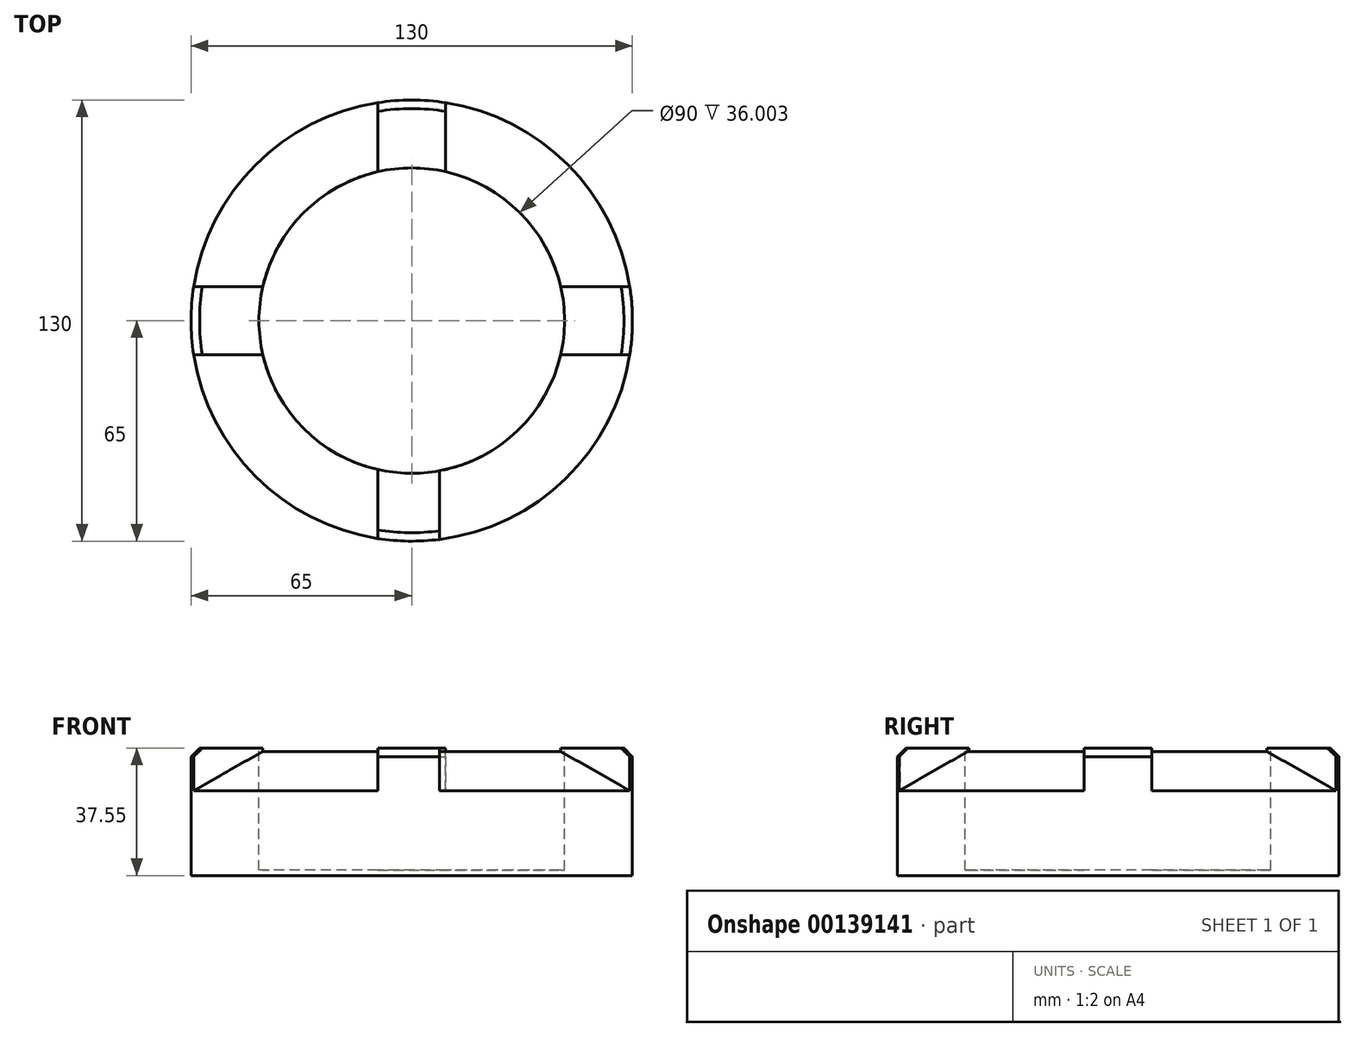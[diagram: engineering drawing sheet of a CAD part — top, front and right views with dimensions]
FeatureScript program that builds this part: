
annotation { "Feature Type Name" : "Feature", "Feature Type Description" : "" }
export const myFeature = defineFeature(function(context is Context, id is Id, definition is map)
    precondition{}
    {
        {
            var Q0;
            Q0=qCreatedBy(makeId("Right.planeOp"),FACE);
            var sketch = newSketch(context, id + "F0", { "sketchPlane" : qUnion([Q0])});
            skLineSegment(sketch, "E0", {"start": v(0, 0) * mm, "end": v(-65, 0) * mm});
            skLineSegment(sketch, "E1", {"start": v(0, 0) * mm, "end": v(-45, 0) * mm});
            skPoint(sketch, "E2", {"position": v(-45, 11.55) * mm});
            skLineSegment(sketch, "E3", {"start": v(-45, 11.55) * mm, "end": v(0, 11.55) * mm});
            skLineSegment(sketch, "E4", {"start": v(0, 11.55) * mm, "end": v(0, 0) * mm});
            skLineSegment(sketch, "E5", {"start": v(-65, 0) * mm, "end": v(-45, 11.55) * mm});
            skSolve(sketch);
        }
        {
            var Q0;
            {var subQ2=sQuery(id+"F0.wireOp",EDGE,"E0");Q0=makeQuery(id+"F0.imprint","IMPRINT",FACE,{"disambiguationData":[TD([[makeQuery(id+"F0.imprint","IMPRINT",EDGE,{"derivedFrom":subQ2}),-1.0]])]});}
            var Q1;
            Q1=sQuery(id+"F0.wireOp",EDGE,"E4");
            revolve(context, id + "F1", {"entities" : qUnion([Q0]), "axis" : qUnion([Q1]), "revolveType" : RevolveType.FULL});
        }
        {
            var Q0;
            Q0=makeQuery(id+"F1.opRevolve","SWEPT_FACE",FACE,{"disambiguationData":[OSD([sQuery(id+"F0.wireOp",EDGE,"E0"),sQuery(id+"F0.wireOp",EDGE,"E1")])]});
            extrude(context, id + "F2", {"entities" : qUnion([Q0]), "operationType" : NewBodyOperationType.ADD, "depth" : 25 * mm});
        }
        {
            var Q0;
            Q0=makeQuery(id+"F1.opRevolve","SWEPT_FACE",FACE,{"disambiguationData":[OSD([sQuery(id+"F0.wireOp",EDGE,"E3")])]});
            extrude(context, id + "F3", {"entities" : qUnion([Q0]), "operationType" : NewBodyOperationType.REMOVE, "oppositeDirection" : true, "depth" : 35 * mm});
        }
        {
            var Q0;
            Q0=makeQuery(id+"F2.opExtrude","CAP_FACE",FACE,{"disambiguationData":[OSD([sQuery(id+"F0.wireOp",EDGE,"E0"),sQuery(id+"F0.wireOp",EDGE,"E1")])],"isStart":false});
            var sketch = newSketch(context, id + "F4", { "sketchPlane" : qUnion([Q0])});
            skLineSegment(sketch, "E6", {"start": v(0, 0) * mm, "end": v(-10, 0) * mm});
            skLineSegment(sketch, "E7", {"start": v(0, 0) * mm, "end": v(0, 10) * mm});
            skLineSegment(sketch, "E8", {"start": v(0, 0) * mm, "end": v(10, 0) * mm});
            skLineSegment(sketch, "E9", {"start": v(0, 0) * mm, "end": v(0, -10) * mm});
            skPoint(sketch, "E10", {"position": v(-65, 0) * mm});
            skPoint(sketch, "E11", {"position": v(65, 0) * mm});
            skPoint(sketch, "E12", {"position": v(0, 65) * mm});
            skPoint(sketch, "E13", {"position": v(0, -65) * mm});
            skLineSegment(sketch, "E14", {"start": v(0, -65) * mm, "end": v(-10, -65) * mm});
            skLineSegment(sketch, "E15", {"start": v(0, -65) * mm, "end": v(10, -65) * mm});
            skLineSegment(sketch, "E16", {"start": v(10, -65) * mm, "end": v(10, -42) * mm});
            skLineSegment(sketch, "E17", {"start": v(-10, -65) * mm, "end": v(-10, -42) * mm});
            skLineSegment(sketch, "E18", {"start": v(-10, -42) * mm, "end": v(10, -42) * mm});
            skLineSegment(sketch, "E19", {"start": v(65, 0) * mm, "end": v(65, 10) * mm});
            skLineSegment(sketch, "E20", {"start": v(65, 0) * mm, "end": v(65, -10) * mm});
            skLineSegment(sketch, "E21", {"start": v(65, 10) * mm, "end": v(42, 10) * mm});
            skLineSegment(sketch, "E22", {"start": v(65, -10) * mm, "end": v(42, -10) * mm});
            skLineSegment(sketch, "E23", {"start": v(42, -10) * mm, "end": v(42, 10) * mm});
            skLineSegment(sketch, "E24", {"start": v(0, 65) * mm, "end": v(-10, 65) * mm});
            skLineSegment(sketch, "E25", {"start": v(0, 65) * mm, "end": v(8.18, 65) * mm});
            skLineSegment(sketch, "E26", {"start": v(8.18, 65) * mm, "end": v(8.18, 42) * mm});
            skLineSegment(sketch, "E27", {"start": v(8.18, 42) * mm, "end": v(-10, 42) * mm});
            skLineSegment(sketch, "E28", {"start": v(-10, 42) * mm, "end": v(-10, 65) * mm});
            skLineSegment(sketch, "E29", {"start": v(-65, 0) * mm, "end": v(-65, 10) * mm});
            skLineSegment(sketch, "E30", {"start": v(-65, 0) * mm, "end": v(-65, -10) * mm});
            skLineSegment(sketch, "E31", {"start": v(-65, -10) * mm, "end": v(-42, -10) * mm});
            skLineSegment(sketch, "E32", {"start": v(-65, 10) * mm, "end": v(-42, 10) * mm});
            skLineSegment(sketch, "E33", {"start": v(-42, 10) * mm, "end": v(-42, -10) * mm});
            skSolve(sketch);
        }
        {
            var Q0;
            {var subQ4=sQuery(id+"F4.wireOp",EDGE,"E33");Q0=makeQuery(id+"F4.imprint","IMPRINT",FACE,{"disambiguationData":[TD([[makeQuery(id+"F4.imprint","IMPRINT",EDGE,{"derivedFrom":subQ4}),-1.0]])]});}
            var Q1;
            {var subQ4=sQuery(id+"F4.wireOp",EDGE,"E18");Q1=makeQuery(id+"F4.imprint","IMPRINT",FACE,{"disambiguationData":[TD([[makeQuery(id+"F4.imprint","IMPRINT",EDGE,{"derivedFrom":subQ4}),-1.0]])]});}
            var Q2;
            {var subQ5=sQuery(id+"F4.wireOp",EDGE,"E27");Q2=makeQuery(id+"F4.imprint","IMPRINT",FACE,{"disambiguationData":[TD([[makeQuery(id+"F4.imprint","IMPRINT",EDGE,{"derivedFrom":subQ5}),-1.0]])]});}
            var Q3;
            {var subQ4=sQuery(id+"F4.wireOp",EDGE,"E23");Q3=makeQuery(id+"F4.imprint","IMPRINT",FACE,{"disambiguationData":[TD([[makeQuery(id+"F4.imprint","IMPRINT",EDGE,{"derivedFrom":subQ4}),-1.0]])]});}
            extrude(context, id + "F5", {"entities" : qUnion([Q0, Q1, Q2, Q3]), "operationType" : NewBodyOperationType.ADD, "oppositeDirection" : true, "depth" : 37.55 * mm});
        }
        {
            var Q0;
            {var subQ0=sQuery(id+"F0.wireOp",EDGE,"E5");var subQ1=sQuery(id+"F0.wireOp",EDGE,"E0");var subQ2=makeQuery(id+"F2.opExtrude","CAP_EDGE",EDGE,{"disambiguationData":[OSD([subQ1,subQ0])],"isStart":false});Q0=makeQuery(id+"F5.opExtrude","CAP_EDGE",EDGE,{"disambiguationData":[OSD([subQ1,subQ0]),TDD([makeQuery(id+"F4.imprint","IMPRINT",EDGE,{"disambiguationData":[TD([[makeQuery(id+"F4.imprint","INTERSECT",VERTEX,{"derivedFrom":[subQ2,sQuery(id+"F4.wireOp",EDGE,"E26")]}),1.0]])],"derivedFrom":subQ2}),makeQuery(id+"F4.imprint","IMPRINT",EDGE,{"disambiguationData":[TD([[makeQuery(id+"F4.imprint","INTERSECT",VERTEX,{"derivedFrom":[subQ2,sQuery(id+"F4.wireOp",EDGE,"E28")]}),-1.0]])],"derivedFrom":subQ2})])],"isStart":false});}
            var Q1;
            {var subQ0=sQuery(id+"F0.wireOp",EDGE,"E5");var subQ1=sQuery(id+"F0.wireOp",EDGE,"E0");var subQ2=makeQuery(id+"F2.opExtrude","CAP_EDGE",EDGE,{"disambiguationData":[OSD([subQ1,subQ0])],"isStart":false});Q1=makeQuery(id+"F5.opExtrude","CAP_EDGE",EDGE,{"disambiguationData":[OSD([subQ1,subQ0]),TDD([makeQuery(id+"F4.imprint","IMPRINT",EDGE,{"disambiguationData":[TD([[makeQuery(id+"F4.imprint","INTERSECT",VERTEX,{"derivedFrom":[subQ2,sQuery(id+"F4.wireOp",EDGE,"E31")]}),-1.0]])],"derivedFrom":subQ2}),makeQuery(id+"F4.imprint","IMPRINT",EDGE,{"disambiguationData":[TD([[makeQuery(id+"F4.imprint","INTERSECT",VERTEX,{"derivedFrom":[subQ2,sQuery(id+"F4.wireOp",EDGE,"E32")]}),1.0]])],"derivedFrom":subQ2})])],"isStart":false});}
            var Q2;
            {var subQ0=sQuery(id+"F0.wireOp",EDGE,"E5");var subQ1=sQuery(id+"F0.wireOp",EDGE,"E0");var subQ2=makeQuery(id+"F2.opExtrude","CAP_EDGE",EDGE,{"disambiguationData":[OSD([subQ1,subQ0])],"isStart":false});Q2=makeQuery(id+"F5.opExtrude","CAP_EDGE",EDGE,{"disambiguationData":[OSD([subQ1,subQ0]),TDD([makeQuery(id+"F4.imprint","IMPRINT",EDGE,{"disambiguationData":[TD([[makeQuery(id+"F4.imprint","INTERSECT",VERTEX,{"derivedFrom":[subQ2,sQuery(id+"F4.wireOp",EDGE,"E16")]}),-1.0]])],"derivedFrom":subQ2}),makeQuery(id+"F4.imprint","IMPRINT",EDGE,{"disambiguationData":[TD([[makeQuery(id+"F4.imprint","INTERSECT",VERTEX,{"derivedFrom":[subQ2,sQuery(id+"F4.wireOp",EDGE,"E17")]}),1.0]])],"derivedFrom":subQ2})])],"isStart":false});}
            var Q3;
            {var subQ0=sQuery(id+"F0.wireOp",EDGE,"E5");var subQ1=sQuery(id+"F0.wireOp",EDGE,"E0");var subQ2=makeQuery(id+"F2.opExtrude","CAP_EDGE",EDGE,{"disambiguationData":[OSD([subQ1,subQ0])],"isStart":false});Q3=makeQuery(id+"F5.opExtrude","CAP_EDGE",EDGE,{"disambiguationData":[OSD([subQ1,subQ0]),TDD([makeQuery(id+"F4.imprint","IMPRINT",EDGE,{"disambiguationData":[TD([[makeQuery(id+"F4.imprint","INTERSECT",VERTEX,{"derivedFrom":[subQ2,sQuery(id+"F4.wireOp",EDGE,"E21")]}),-1.0]])],"derivedFrom":subQ2}),makeQuery(id+"F4.imprint","IMPRINT",EDGE,{"disambiguationData":[TD([[makeQuery(id+"F4.imprint","INTERSECT",VERTEX,{"derivedFrom":[subQ2,sQuery(id+"F4.wireOp",EDGE,"E22")]}),1.0]])],"derivedFrom":subQ2})])],"isStart":false});}
            chamfer(context, id + "F6", {"entities" : qUnion([Q0, Q1, Q2, Q3]), "width" : 2.5 * mm, "tangentPropagation" : true});
        }
        {
            var Q0;
            Q0=makeQuery(id+"F5.opExtrude","CAP_FACE",FACE,{"disambiguationData":[OSD([sQuery(id+"F0.wireOp",EDGE,"E0"),sQuery(id+"F0.wireOp",EDGE,"E5"),sQuery(id+"F4.wireOp",EDGE,"E21"),sQuery(id+"F4.wireOp",EDGE,"E22"),sQuery(id+"F4.wireOp",EDGE,"E23")])],"isStart":false});
            var sketch = newSketch(context, id + "F7", { "sketchPlane" : qUnion([Q0])});
            skCircle(sketch, "E34", {"center": v(0, 0) * mm, "radius": 45 * mm});
            skSolve(sketch);
        }
        {
            var Q0;
            {var subQ5=makeQuery(id+"F5.opExtrude","CAP_EDGE",EDGE,{"disambiguationData":[OSD([sQuery(id+"F4.wireOp",EDGE,"E23")])],"isStart":false});Q0=makeQuery(id+"F7.imprint","IMPRINT",FACE,{"disambiguationData":[TD([[makeQuery(id+"F7.imprint","IMPRINT",EDGE,{"derivedFrom":subQ5}),-1.0]])]});}
            extrude(context, id + "F8", {"entities" : qUnion([Q0]), "operationType" : NewBodyOperationType.REMOVE, "oppositeDirection" : true, "depth" : 36 * mm});
        }
        {
            var Q0;
            Q0=makeQuery(id+"F5.opExtrude","CAP_FACE",FACE,{"disambiguationData":[OSD([sQuery(id+"F0.wireOp",EDGE,"E0"),sQuery(id+"F0.wireOp",EDGE,"E5"),sQuery(id+"F4.wireOp",EDGE,"E21"),sQuery(id+"F4.wireOp",EDGE,"E22"),sQuery(id+"F4.wireOp",EDGE,"E23")])],"isStart":false});
            var sketch = newSketch(context, id + "F9", { "sketchPlane" : qUnion([Q0])});
            skCircle(sketch, "E35", {"center": v(0, 0) * mm, "radius": 45 * mm});
            skSolve(sketch);
        }
        {
            var Q0;
            {var subQ5=makeQuery(id+"F5.opExtrude","CAP_EDGE",EDGE,{"disambiguationData":[OSD([sQuery(id+"F4.wireOp",EDGE,"E23")])],"isStart":false});Q0=makeQuery(id+"F9.imprint","IMPRINT",FACE,{"disambiguationData":[TD([[makeQuery(id+"F9.imprint","IMPRINT",EDGE,{"derivedFrom":subQ5}),1.0]])]});}
            extrude(context, id + "F10", {"entities" : qUnion([Q0]), "operationType" : NewBodyOperationType.REMOVE, "oppositeDirection" : true, "depth" : 36 * mm});
        }
    });
